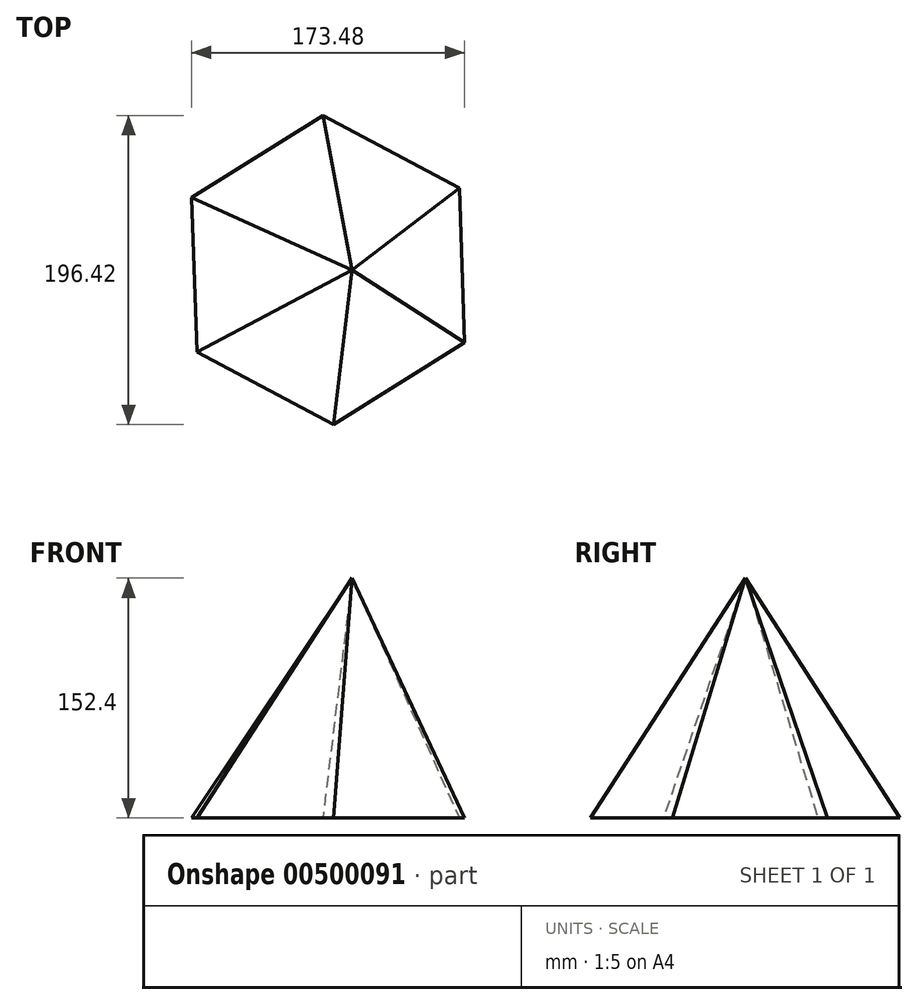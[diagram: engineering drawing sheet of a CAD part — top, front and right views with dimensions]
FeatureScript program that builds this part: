
annotation { "Feature Type Name" : "Feature", "Feature Type Description" : "" }
export const myFeature = defineFeature(function(context is Context, id is Id, definition is map)
    precondition{}
    {
        {
            var Q0;
            Q0=qCreatedBy(makeId("Top.planeOp"),FACE);
            var sketch = newSketch(context, id + "F0", { "sketchPlane" : qUnion([Q0])});
            skCircle(sketch, "E0.cCircle", {"center": v(0, 0) * mm, "radius": 98.27 * mm, "construction": true});
            skLineSegment(sketch, "E0.0", {"start": v(83.36, 52.03) * mm, "end": v(86.74, -46.18) * mm});
            skLineSegment(sketch, "E0.1", {"start": v(86.74, -46.18) * mm, "end": v(3.38, -98.2) * mm});
            skLineSegment(sketch, "E0.2", {"start": v(3.38, -98.2) * mm, "end": v(-83.36, -52.03) * mm});
            skLineSegment(sketch, "E0.3", {"start": v(-83.36, -52.03) * mm, "end": v(-86.74, 46.18) * mm});
            skLineSegment(sketch, "E0.4", {"start": v(-86.74, 46.18) * mm, "end": v(-3.38, 98.2) * mm});
            skLineSegment(sketch, "E0.5", {"start": v(-3.38, 98.2) * mm, "end": v(83.36, 52.03) * mm});
            skSolve(sketch);
        }
        {
            var Q0;
            Q0=qCreatedBy(makeId("Top.planeOp"),FACE);
            cPlane(context, id + "F1", {"entities" : qUnion([Q0]), "cplaneType" : CPlaneType.OFFSET, "offset" : 152.4 * mm, "width" : 152.4 * mm, "height" : 152.4 * mm});
        }
        {
            var Q0;
            Q0=qCreatedBy(id+"F1.planeOp",FACE);
            var sketch = newSketch(context, id + "F2", { "sketchPlane" : qUnion([Q0])});
            skPoint(sketch, "E1", {"position": v(15.2, 0) * mm});
            skSolve(sketch);
        }
        {
            var Q0;
            Q0=sQuery(id+"F2.wireOp",VERTEX,"E1");
            var Q1;
            Q1=makeQuery(id+"F0.imprint","IMPRINT",FACE,{"disambiguationData":[TD([[makeQuery(id+"F0.imprint","IMPRINT",EDGE,{"derivedFrom":sQuery(id+"F0.wireOp",EDGE,"E0.0")}),-1.0]])]});
            loft(context, id + "F3", {"sheetProfilesArray" : [{ "sheetProfileEntities" : qUnion([Q0]) }, { "sheetProfileEntities" : qUnion([Q1]) }]});
        }
    });
